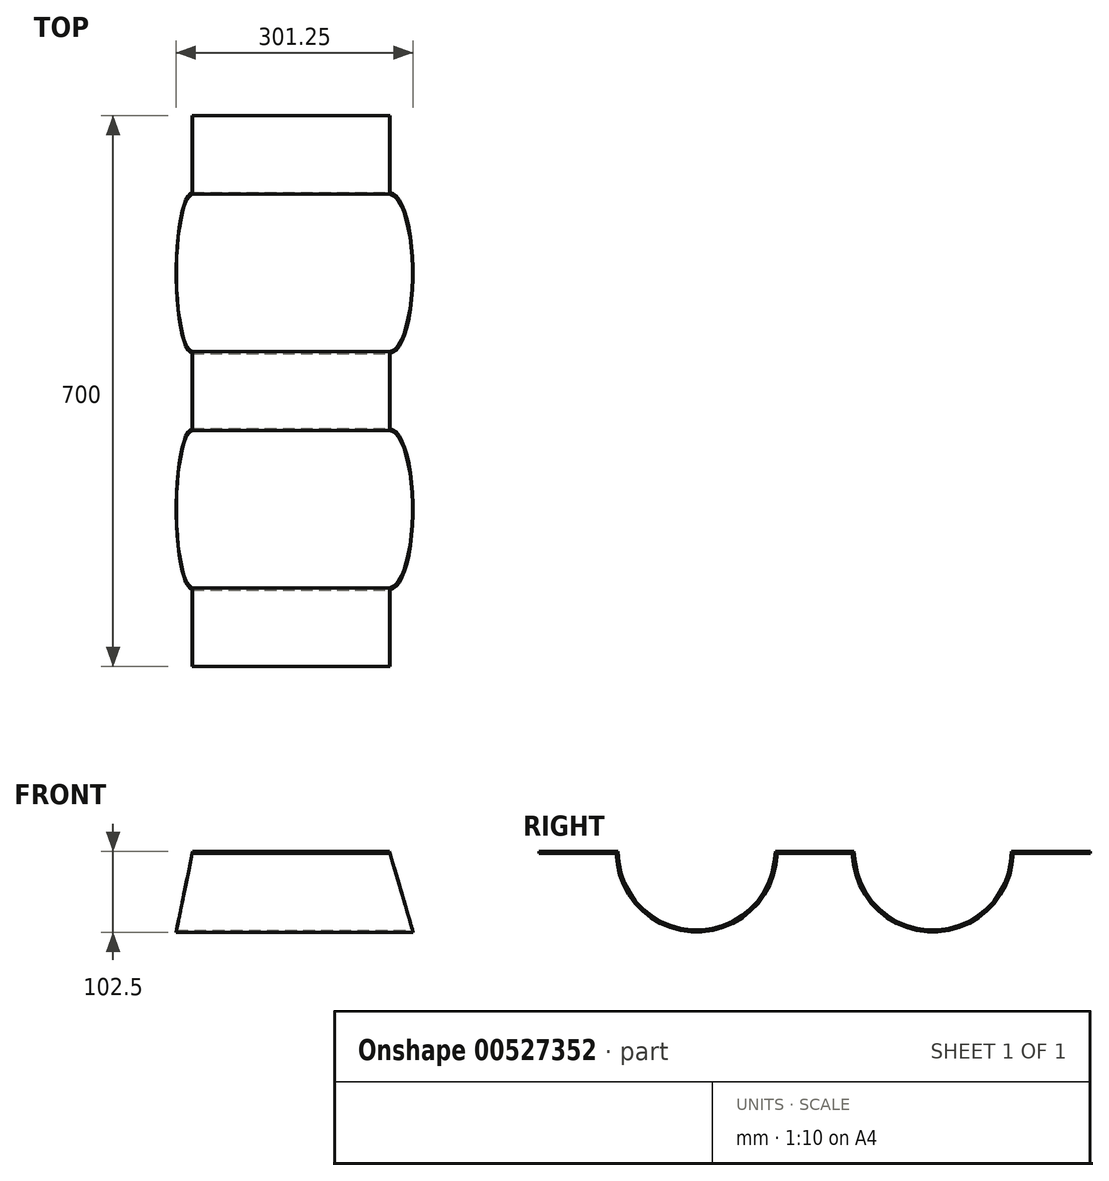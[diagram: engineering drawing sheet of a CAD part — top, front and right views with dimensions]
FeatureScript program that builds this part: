
annotation { "Feature Type Name" : "Feature", "Feature Type Description" : "" }
export const myFeature = defineFeature(function(context is Context, id is Id, definition is map)
    precondition{}
    {
        {
            var Q0;
            Q0=qCreatedBy(makeId("Front.planeOp"),FACE);
            var sketch = newSketch(context, id + "F0", { "sketchPlane" : qUnion([Q0])});
            skLineSegment(sketch, "E0", {"start": v(124.12, 332.38) * mm, "end": v(-125.88, 332.38) * mm});
            skLineSegment(sketch, "E1", {"start": v(-125.88, 332.38) * mm, "end": v(-229.3, -167.62) * mm});
            skLineSegment(sketch, "E2", {"start": v(-229.3, -167.62) * mm, "end": v(270.7, -167.62) * mm});
            skLineSegment(sketch, "E3", {"start": v(270.7, -167.62) * mm, "end": v(124.12, 332.38) * mm});
            skSolve(sketch);
        }
        {
            var Q0;
            Q0=qSketchRegion(id+"F0",true);
            extrude(context, id + "F1", {"entities" : qUnion([Q0]), "oppositeDirection" : true, "depth" : 700 * mm, "offsetDistance" : 25 * mm});
        }
        {
            var Q0;
            Q0=qCreatedBy(makeId("Right.planeOp"),FACE);
            var sketch = newSketch(context, id + "F2", { "sketchPlane" : qUnion([Q0])});
            skCircle(sketch, "E4", {"center": v(200, 332.38) * mm, "radius": 100 * mm});
            skCircle(sketch, "E5", {"center": v(500, 332.38) * mm, "radius": 100 * mm});
            skSolve(sketch);
        }
        {
            var Q0;
            Q0=qSketchRegion(id+"F2",true);
            extrude(context, id + "F3", {"entities" : qUnion([Q0]), "operationType" : NewBodyOperationType.REMOVE, "oppositeDirection" : true, "depth" : 400 * mm, "offsetDistance" : 25 * mm, "hasSecondDirection" : true, "secondDirectionOppositeDirection" : false, "secondDirectionDepth" : 310 * mm});
        }
        {
            var Q0;
            Q0=makeQuery(id+"F1.opExtrude","CAP_FACE",FACE,{"disambiguationData":[OSD([sQuery(id+"F0.wireOp",EDGE,"E0"),sQuery(id+"F0.wireOp",EDGE,"E1"),sQuery(id+"F0.wireOp",EDGE,"E2"),sQuery(id+"F0.wireOp",EDGE,"E3")])],"isStart":true});
            var Q1;
            Q1=makeQuery(id+"F1.opExtrude","SWEPT_FACE",FACE,{"disambiguationData":[OSD([sQuery(id+"F0.wireOp",EDGE,"E3")])]});
            var Q2;
            Q2=makeQuery(id+"F1.opExtrude","SWEPT_FACE",FACE,{"disambiguationData":[OSD([sQuery(id+"F0.wireOp",EDGE,"E2")])]});
            var Q3;
            Q3=makeQuery(id+"F1.opExtrude","SWEPT_FACE",FACE,{"disambiguationData":[OSD([sQuery(id+"F0.wireOp",EDGE,"E1")])]});
            var Q4;
            Q4=makeQuery(id+"F1.opExtrude","CAP_FACE",FACE,{"disambiguationData":[OSD([sQuery(id+"F0.wireOp",EDGE,"E0"),sQuery(id+"F0.wireOp",EDGE,"E1"),sQuery(id+"F0.wireOp",EDGE,"E2"),sQuery(id+"F0.wireOp",EDGE,"E3")])],"isStart":false});
            shell(context, id + "F4", {"entities" : qUnion([Q0, Q1, Q2, Q3, Q4]), "thickness" : 2.5 * mm});
        }
    });
